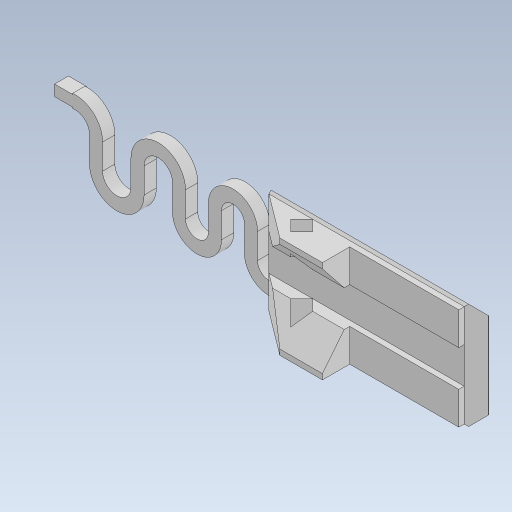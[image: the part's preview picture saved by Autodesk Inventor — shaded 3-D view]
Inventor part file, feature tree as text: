
AUTODESK INVENTOR PART (.ipt)
format: ipt  version: 2023 (Build 270158030, 158C)  size: 194,048 bytes
history: native  units: mm
features: other x4, chamfer x1
ambient origin geometry x8: Origin, YZ Plane, XZ Plane, XY Plane, X Axis, Y Axis, Z Axis, Center Point
bodies: Body1 (feature_tree)
feature tree (5):
  other  "v4-latch.ipt"
  chamfer  "Chamfer1"  Distance=10.0mm
  other  "slide::v4-latch.ipt"
  other  "TaggingFeature1"
  other  "slide"
